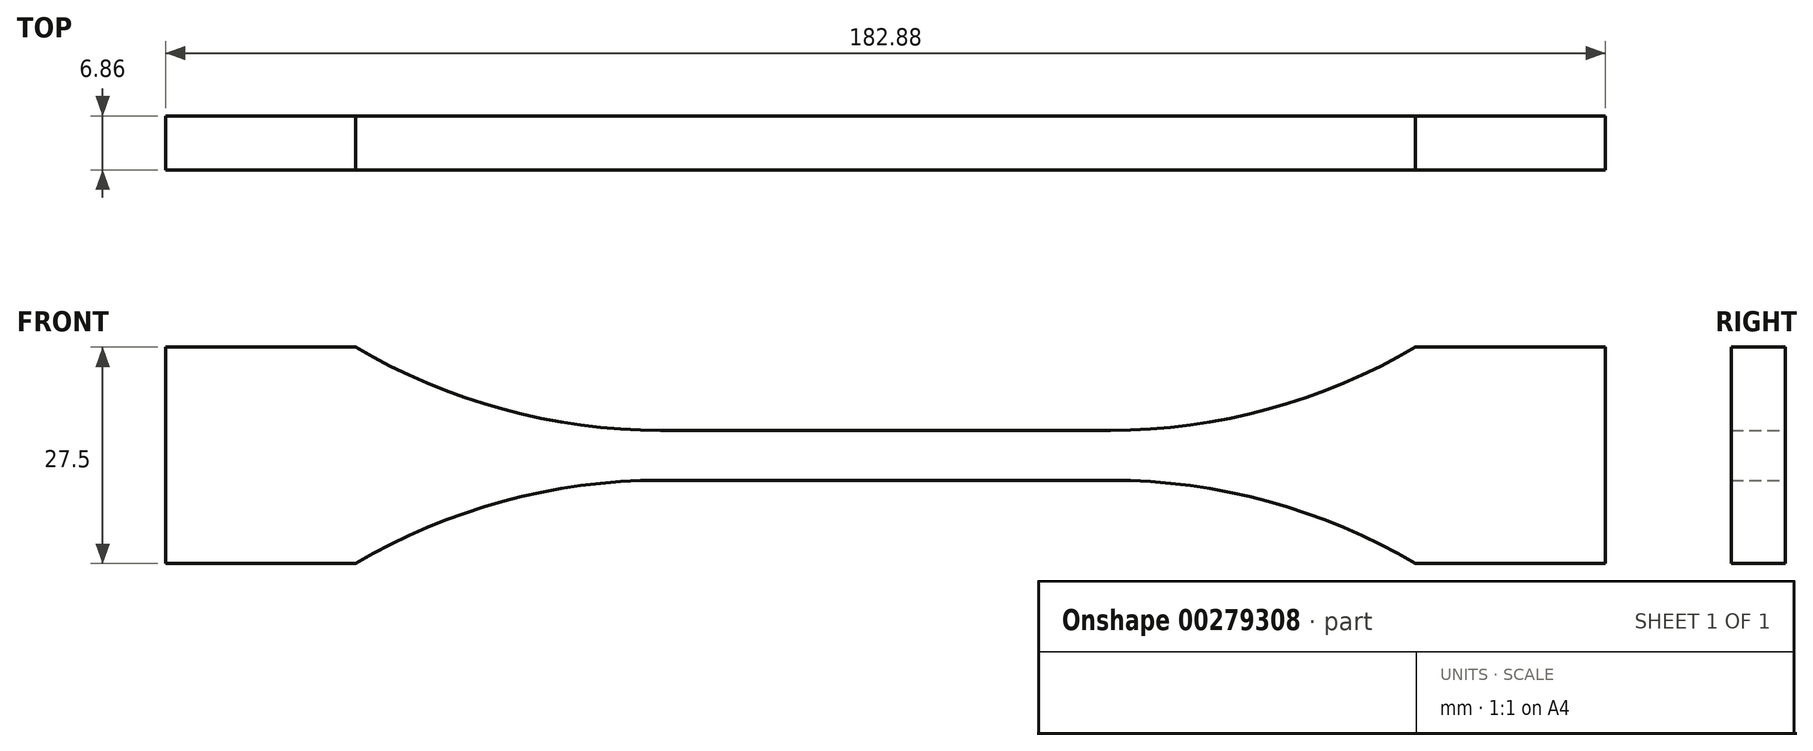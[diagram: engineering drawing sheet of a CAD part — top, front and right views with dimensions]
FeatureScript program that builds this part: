
annotation { "Feature Type Name" : "Feature", "Feature Type Description" : "" }
export const myFeature = defineFeature(function(context is Context, id is Id, definition is map)
    precondition{}
    {
        {
            var Q0;
            Q0=qCreatedBy(makeId("Front.planeOp"),FACE);
            var sketch = newSketch(context, id + "F0", { "sketchPlane" : qUnion([Q0])});
            skLineSegment(sketch, "E0", {"start": v(0, 3.18) * mm, "end": v(28.58, 3.18) * mm});
            skArc(sketch, "E1", {"start": v(28.58, 3.17) * mm, "mid": v(48.65, 5.87) * mm, "end": v(67.31, 13.75) * mm});
            skLineSegment(sketch, "E2", {"start": v(67.31, 13.75) * mm, "end": v(91.44, 13.75) * mm});
            skArc(sketch, "E3.MirrorCS", {"start": v(28.58, -3.17) * mm, "mid": v(48.65, -5.87) * mm, "end": v(67.31, -13.75) * mm});
            skLineSegment(sketch, "E4.MirrorCS", {"start": v(67.31, -13.75) * mm, "end": v(91.44, -13.75) * mm});
            skLineSegment(sketch, "E5.MirrorCS", {"start": v(0, -3.18) * mm, "end": v(28.58, -3.18) * mm});
            skLineSegment(sketch, "E6.MirrorCS", {"start": v(-67.31, -13.75) * mm, "end": v(-91.44, -13.75) * mm});
            skLineSegment(sketch, "E7.MirrorCS", {"start": v(-67.31, 13.75) * mm, "end": v(-91.44, 13.75) * mm});
            skArc(sketch, "E8.MirrorCS", {"start": v(-28.58, -3.17) * mm, "mid": v(-48.65, -5.87) * mm, "end": v(-67.31, -13.75) * mm});
            skArc(sketch, "E9.MirrorCS", {"start": v(-28.58, 3.17) * mm, "mid": v(-48.65, 5.87) * mm, "end": v(-67.31, 13.75) * mm});
            skLineSegment(sketch, "E10.MirrorCS", {"start": v(0, -3.17) * mm, "end": v(-28.58, -3.17) * mm});
            skLineSegment(sketch, "E11.MirrorCS", {"start": v(0, 3.18) * mm, "end": v(-28.58, 3.18) * mm});
            skLineSegment(sketch, "E12", {"start": v(-91.44, 13.75) * mm, "end": v(-91.44, -13.75) * mm});
            skLineSegment(sketch, "E13", {"start": v(91.44, 13.75) * mm, "end": v(91.44, -13.75) * mm});
            skSolve(sketch);
        }
        {
            var Q0;
            Q0=makeQuery(id+"F0.imprint","IMPRINT",FACE,{"disambiguationData":[TD([[makeQuery(id+"F0.imprint","IMPRINT",EDGE,{"derivedFrom":sQuery(id+"F0.wireOp",EDGE,"E0")}),-1.0]])]});
            extrude(context, id + "F1", {"entities" : qUnion([Q0]), "depth" : 6.86 * mm});
        }
    });
